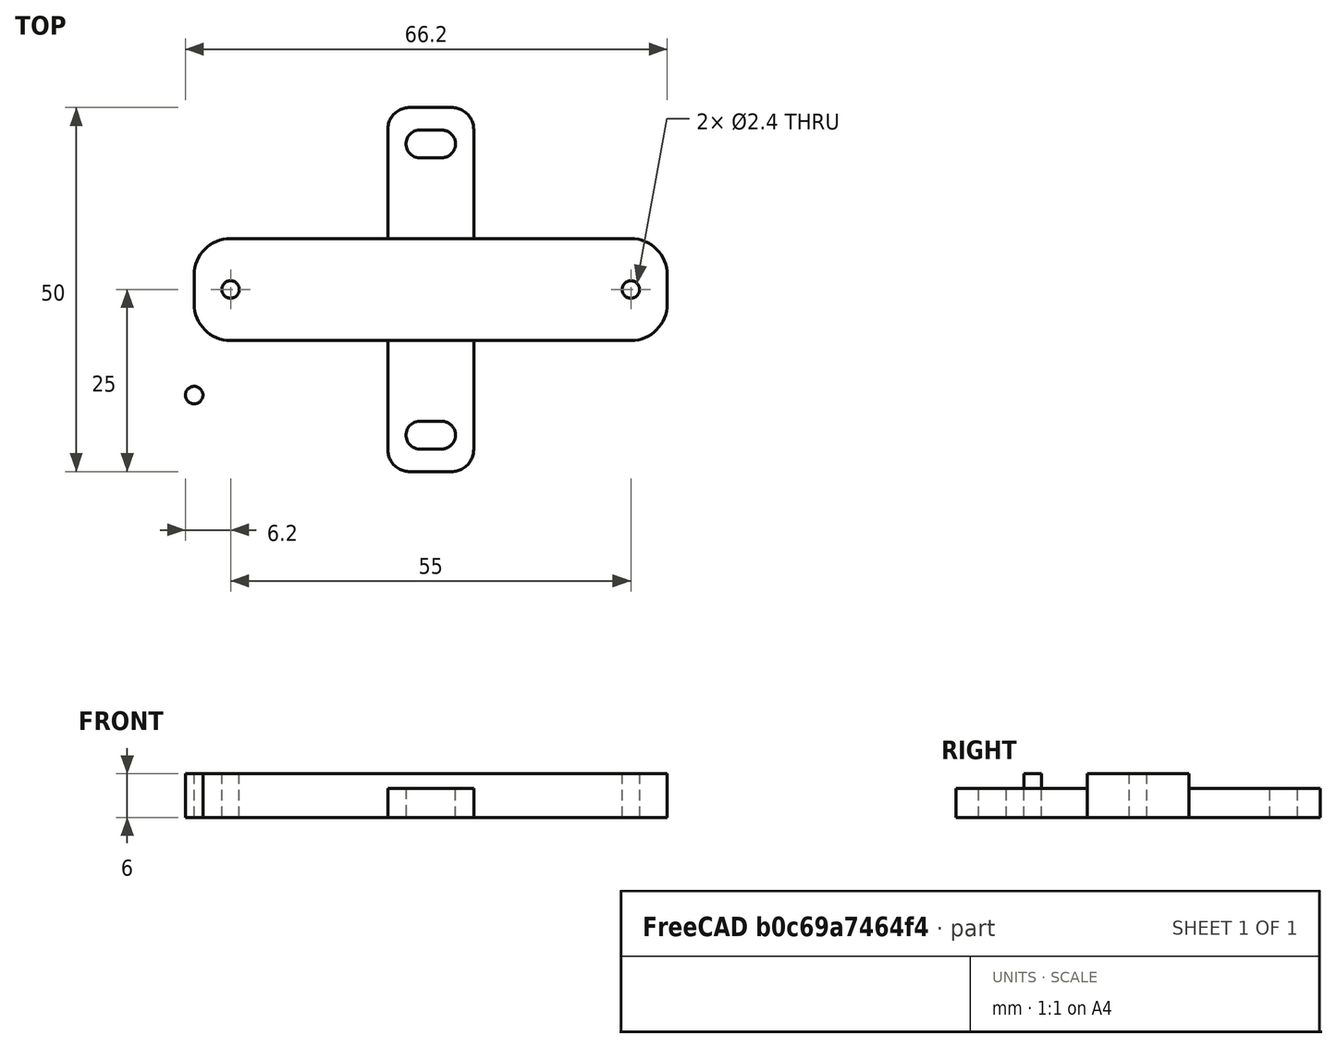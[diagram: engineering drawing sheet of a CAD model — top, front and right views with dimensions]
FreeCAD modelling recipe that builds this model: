
FCSTD DOCUMENT  (FreeCAD 0.19R23578 (Git))
Label: blm_26650_acc
License: All rights reserved
LicenseURL: http://en.wikipedia.org/wiki/All_rights_reserved
objects: Part::FeaturePython×2, Part::Box×1, Spreadsheet::Sheet×1, Part::Cylinder×1, Part::Feature×1, Part::Fillet×1, Part::Cut×1, Part::MultiFuse×1, App::Part×1
note: 7 computed .brp shape members not serialized (recipe doc carries the construction recipe); baked Part::Feature solids carry a one-line shape summary decoded from their .brp

FEATURE [Part::Box] Box  label="plate cube"
  AttacherType = Attacher::AttachEngine3D
  Height = 6
  Length = 65
  Width = 14
  expr: Height = <<p>>.plate_z
  expr: Width = <<p>>.plate_y
  expr: Length = <<p>>.plate_x
FEATURE [Spreadsheet::Sheet] Spreadsheet  label="p"
  cells = A1=hole_dist_x; B1(hole_dist_x)==55mm; A2=hole_r; B2(hole_r)==1.2mm; A3=plate_x; B3(plate_x)==65mm; A4=plate_y; B4(plate_y)==14mm; A5=plate_z; B5(plate_z)==6mm; A6=box_y; B6(box_y)==29mm
FEATURE [Part::Cylinder] Cylinder  label="screw_hole"
  Angle = 360
  AttacherType = Attacher::AttachEngine3D
  Height = 6
  Radius = 1.2
  expr: Radius = <<p>>.hole_r
  expr: Height = <<p>>.plate_z
FEATURE [Part::FeaturePython] Array  label="screw hole array"  # Draft array (typed FeaturePython)
  Angle = 360
  ArrayType = 0
  Axis = (0,0,1)
  Base = -> Cylinder
  Center = (0,0,0)
  Count = 2
  ExpandArray = false
  Fuse = false
  IntervalAxis = (0,0,0)
  IntervalX = (55,0,0)
  IntervalY = (0,100,0)
  IntervalZ = (0,0,100)
  NumberCircles = 3
  NumberPolar = 5
  NumberX = 2
  NumberY = 1
  NumberZ = 1
  Placement = pos=(5,7,0) rot=(0,0,1;0rad)
  PlacementList = 2 placements: [(0,0,0),(55,0,0)]
  RadialDistance = 50
  ScaleList = (2) [(1,1,1),(1,1,1)]
  Symmetry = 1
  TangentialDistance = 25
  expr: .IntervalX.x = <<p>>.hole_dist_x
  expr: .Placement.Base.x = (<<p>>.plate_x - <<p>>.hole_dist_x) / 2
  expr: .Placement.Base.y = <<p>>.plate_y / 2
FEATURE [Part::Feature] Cut002001  label="attach plane y dir001"
  Placement = pos=(26.6,-10.5,0) rot=(0,0,1;0rad)
  shape: bbox 11.8 x 50 x 2 mm, 20 faces (baked)
FEATURE [Part::Fillet] Fillet  label="plate fillet"
  Base = -> Box
  Edges = 4 edges r=5: [Edge1,Edge3,Edge5,Edge7]
FEATURE [Part::Cut] Cut  label="body cut"
  Base = -> Fillet
  Placement = pos=(0,7.5,0) rot=(0,0,1;0rad)
  Tool = -> Array
  expr: .Placement.Base.y = (<<p>>.box_y - <<p>>.plate_y) / 2
FEATURE [Part::FeaturePython] Clone  label="attach plane y scaled"  # Draft clone (typed FeaturePython)
  AttacherType = Attacher::AttachEngine3D
  Fuse = false
  Objects = -> [Cut002001]
  Placement = pos=(26.6,-10.5,0) rot=(0,0,1;0rad)
  Scale = (1,1,2)
FEATURE [Part::MultiFuse] Fusion  label="body fusion"
  Shapes = -> [Cut,Clone]
FEATURE [App::Part] Part  label="acc 26650 part"
  Group = -> [Cut002001,Cylinder,Array,Box,Fillet,Cut,Fusion]
  Origin = -> Origin
